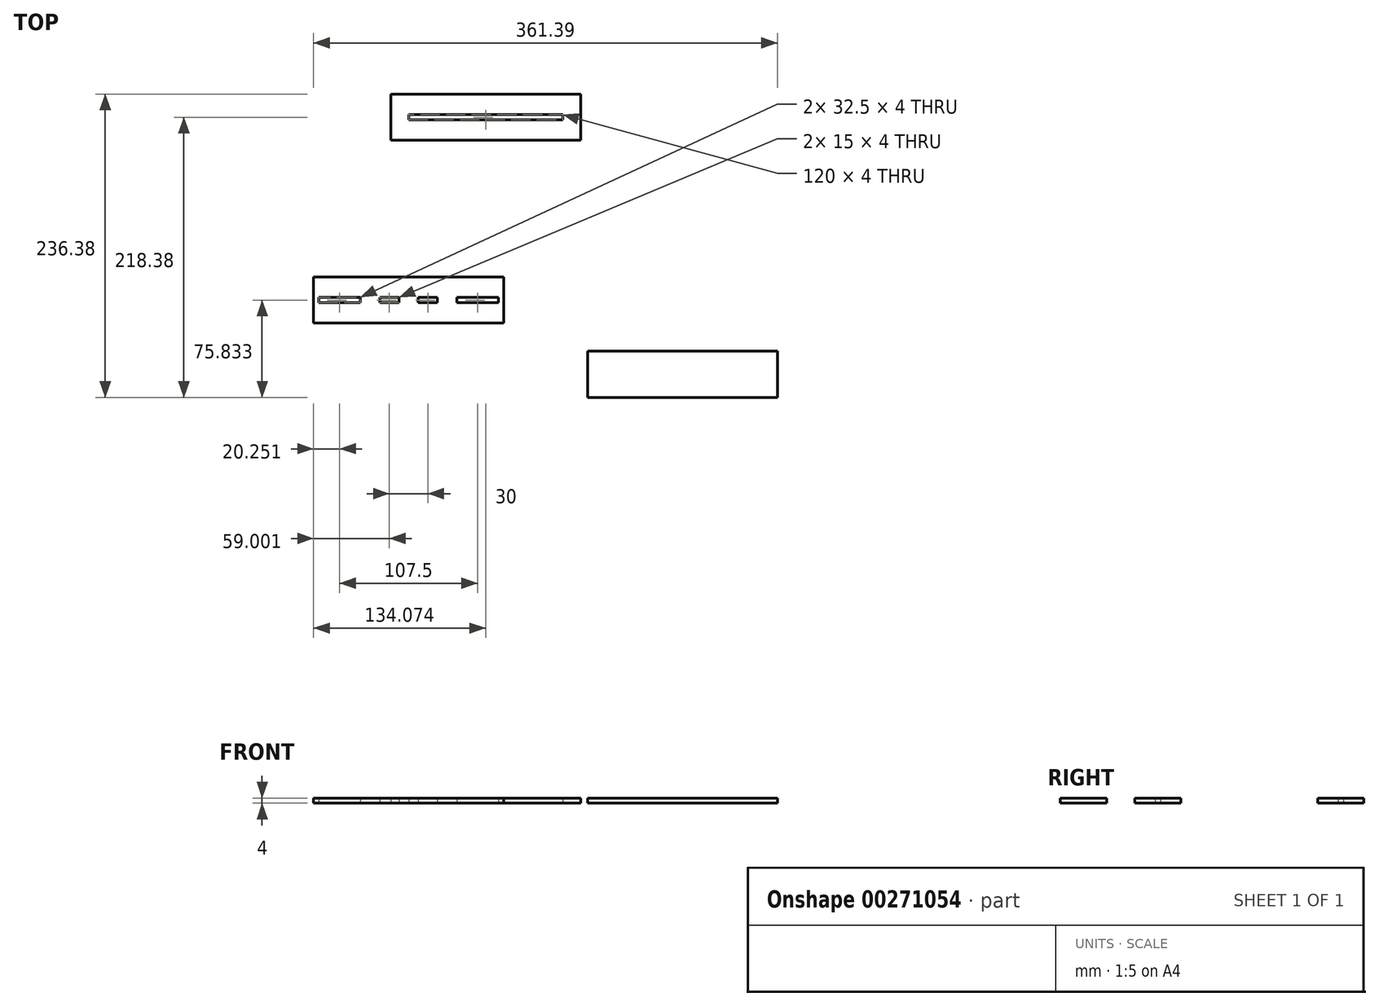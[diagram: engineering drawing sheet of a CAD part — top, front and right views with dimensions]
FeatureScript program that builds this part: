
annotation { "Feature Type Name" : "Feature", "Feature Type Description" : "" }
export const myFeature = defineFeature(function(context is Context, id is Id, definition is map)
    precondition{}
    {
        {
            var Q0;
            Q0=qCreatedBy(makeId("Top.planeOp"),FACE);
            var sketch = newSketch(context, id + "F0", { "sketchPlane" : qUnion([Q0])});
            skLineSegment(sketch, "E0", {"start": v(6.67, -14.36) * mm, "end": v(-141.33, -14.36) * mm});
            skLineSegment(sketch, "E1", {"start": v(-141.33, -50.36) * mm, "end": v(6.67, -50.36) * mm});
            skLineSegment(sketch, "E2", {"start": v(-141.33, -14.36) * mm, "end": v(-141.33, -30.36) * mm});
            skLineSegment(sketch, "E3", {"start": v(-141.33, -30.36) * mm, "end": v(-141.33, -34.36) * mm});
            skLineSegment(sketch, "E4", {"start": v(-141.33, -34.36) * mm, "end": v(-141.33, -50.36) * mm});
            skLineSegment(sketch, "E5", {"start": v(6.67, -14.36) * mm, "end": v(6.67, -30.36) * mm});
            skLineSegment(sketch, "E6", {"start": v(6.67, -30.36) * mm, "end": v(6.67, -34.36) * mm});
            skLineSegment(sketch, "E7", {"start": v(6.67, -34.36) * mm, "end": v(6.67, -50.36) * mm});
            skLineSegment(sketch, "E8", {"start": v(-104.83, -30.36) * mm, "end": v(-104.83, -30.36) * mm});
            skLineSegment(sketch, "E9", {"start": v(-89.83, -30.36) * mm, "end": v(-74.83, -30.36) * mm});
            skLineSegment(sketch, "E10", {"start": v(-29.83, -30.36) * mm, "end": v(2.67, -30.36) * mm});
            skLineSegment(sketch, "E11", {"start": v(-137.33, -30.36) * mm, "end": v(-137.33, -34.36) * mm});
            skLineSegment(sketch, "E12", {"start": v(-104.83, -30.36) * mm, "end": v(-104.83, -34.36) * mm});
            skLineSegment(sketch, "E13", {"start": v(-89.83, -30.36) * mm, "end": v(-89.83, -34.36) * mm});
            skLineSegment(sketch, "E14", {"start": v(-74.83, -30.36) * mm, "end": v(-74.83, -34.36) * mm});
            skLineSegment(sketch, "E15", {"start": v(-59.83, -30.36) * mm, "end": v(-59.83, -34.36) * mm});
            skLineSegment(sketch, "E16", {"start": v(-44.83, -30.36) * mm, "end": v(-44.83, -34.36) * mm});
            skLineSegment(sketch, "E17", {"start": v(-29.83, -30.36) * mm, "end": v(-29.83, -34.36) * mm});
            skLineSegment(sketch, "E18", {"start": v(2.67, -30.36) * mm, "end": v(2.67, -34.36) * mm});
            skLineSegment(sketch, "E19", {"start": v(-137.33, -30.36) * mm, "end": v(-104.83, -30.36) * mm});
            skLineSegment(sketch, "E20", {"start": v(-137.33, -34.36) * mm, "end": v(-104.83, -34.36) * mm});
            skLineSegment(sketch, "E21", {"start": v(-89.83, -34.36) * mm, "end": v(-74.83, -34.36) * mm});
            skLineSegment(sketch, "E22", {"start": v(-44.83, -34.36) * mm, "end": v(-59.83, -34.36) * mm});
            skLineSegment(sketch, "E23", {"start": v(-59.83, -30.36) * mm, "end": v(-44.83, -30.36) * mm});
            skLineSegment(sketch, "E24", {"start": v(-29.83, -34.36) * mm, "end": v(2.67, -34.36) * mm});
            skSolve(sketch);
        }
        {
            var Q0;
            Q0 = qSketchRegion(id + "F0", true);
            extrude(context, id + "F1", {"entities" : qUnion([Q0]), "depth" : 4 * mm});
        }
        {
            var Q0;
            Q0=qCreatedBy(makeId("Top.planeOp"),FACE);
            var sketch = newSketch(context, id + "F2", { "sketchPlane" : qUnion([Q0])});
            skLineSegment(sketch, "E25", {"start": v(66.74, 128.2) * mm, "end": v(-81.26, 128.2) * mm});
            skLineSegment(sketch, "E26", {"start": v(-81.26, 92.2) * mm, "end": v(66.74, 92.2) * mm});
            skLineSegment(sketch, "E27", {"start": v(-81.26, 128.2) * mm, "end": v(-81.26, 112.2) * mm});
            skLineSegment(sketch, "E28", {"start": v(-81.26, 112.2) * mm, "end": v(-81.26, 108.2) * mm});
            skLineSegment(sketch, "E29", {"start": v(-81.26, 108.2) * mm, "end": v(-81.26, 92.2) * mm});
            skLineSegment(sketch, "E30", {"start": v(66.74, 128.2) * mm, "end": v(66.74, 112.2) * mm});
            skLineSegment(sketch, "E31", {"start": v(66.74, 112.2) * mm, "end": v(66.74, 108.2) * mm});
            skLineSegment(sketch, "E32", {"start": v(66.74, 108.2) * mm, "end": v(66.74, 92.2) * mm});
            skLineSegment(sketch, "E33", {"start": v(-67.26, 112.2) * mm, "end": v(52.74, 112.2) * mm});
            skLineSegment(sketch, "E34", {"start": v(52.74, 108.2) * mm, "end": v(-67.26, 108.2) * mm});
            skLineSegment(sketch, "E35", {"start": v(-67.26, 112.2) * mm, "end": v(-67.26, 108.2) * mm});
            skLineSegment(sketch, "E36", {"start": v(52.74, 112.2) * mm, "end": v(52.74, 108.2) * mm});
            skSolve(sketch);
        }
        {
            var Q0;
            Q0=makeQuery(id+"F2.imprint","IMPRINT",FACE,{"disambiguationData":[TD([[makeQuery(id+"F2.imprint","IMPRINT",EDGE,{"derivedFrom":sQuery(id+"F2.wireOp",EDGE,"E25")}),1.0]])]});
            extrude(context, id + "F3", {"entities" : qUnion([Q0]), "depth" : 4 * mm});
        }
        {
            var Q0;
            Q0=qCreatedBy(makeId("Top.planeOp"),FACE);
            var sketch = newSketch(context, id + "F4", { "sketchPlane" : qUnion([Q0])});
            skLineSegment(sketch, "E37", {"start": v(220.06, -72.2) * mm, "end": v(72.06, -72.2) * mm});
            skLineSegment(sketch, "E38", {"start": v(72.06, -72.2) * mm, "end": v(72.06, -108.2) * mm});
            skLineSegment(sketch, "E39", {"start": v(72.06, -108.2) * mm, "end": v(220.06, -108.2) * mm});
            skLineSegment(sketch, "E40", {"start": v(220.06, -108.2) * mm, "end": v(220.06, -72.2) * mm});
            skSolve(sketch);
        }
        {
            var Q0;
            Q0=makeQuery(id+"F4.imprint","IMPRINT",FACE,{"disambiguationData":[TD([[makeQuery(id+"F4.imprint","IMPRINT",EDGE,{"derivedFrom":sQuery(id+"F4.wireOp",EDGE,"E37")}),1.0]])]});
            extrude(context, id + "F5", {"entities" : qUnion([Q0]), "depth" : 4 * mm});
        }
    });
